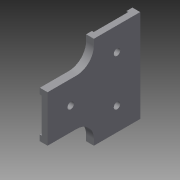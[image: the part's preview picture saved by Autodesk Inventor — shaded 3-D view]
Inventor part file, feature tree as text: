
AUTODESK INVENTOR PART (.ipt)
format: ipt  version: 2015 (Build 190159000, 159)  size: 118,784 bytes
history: native  units: in
note: dims shown in document units (in); Inventor stores cm internally (conversion verified against a paired STEP export)
features: extrude x2, sketch x2, projected_geometry x1
ambient origin geometry x8: Origin, YZ Plane, XZ Plane, XY Plane, X Axis, Y Axis, Z Axis, Center Point
bodies: Solid1 (feature_tree)
feature tree (5):
  extrude  "Extrusion1"  Depth=0.75in
  extrude  "Extrusion2"  Depth=0.0394in TaperAngle=0.0deg
  sketch  "Sketch1"  dims[d0=0.128in d1=0.0in d2=0.75in]
  sketch  "Sketch2"  dims[d3=0.75in d4=0.0394in d5=0.0in]
  projected_geometry  "Projected Loop1"
